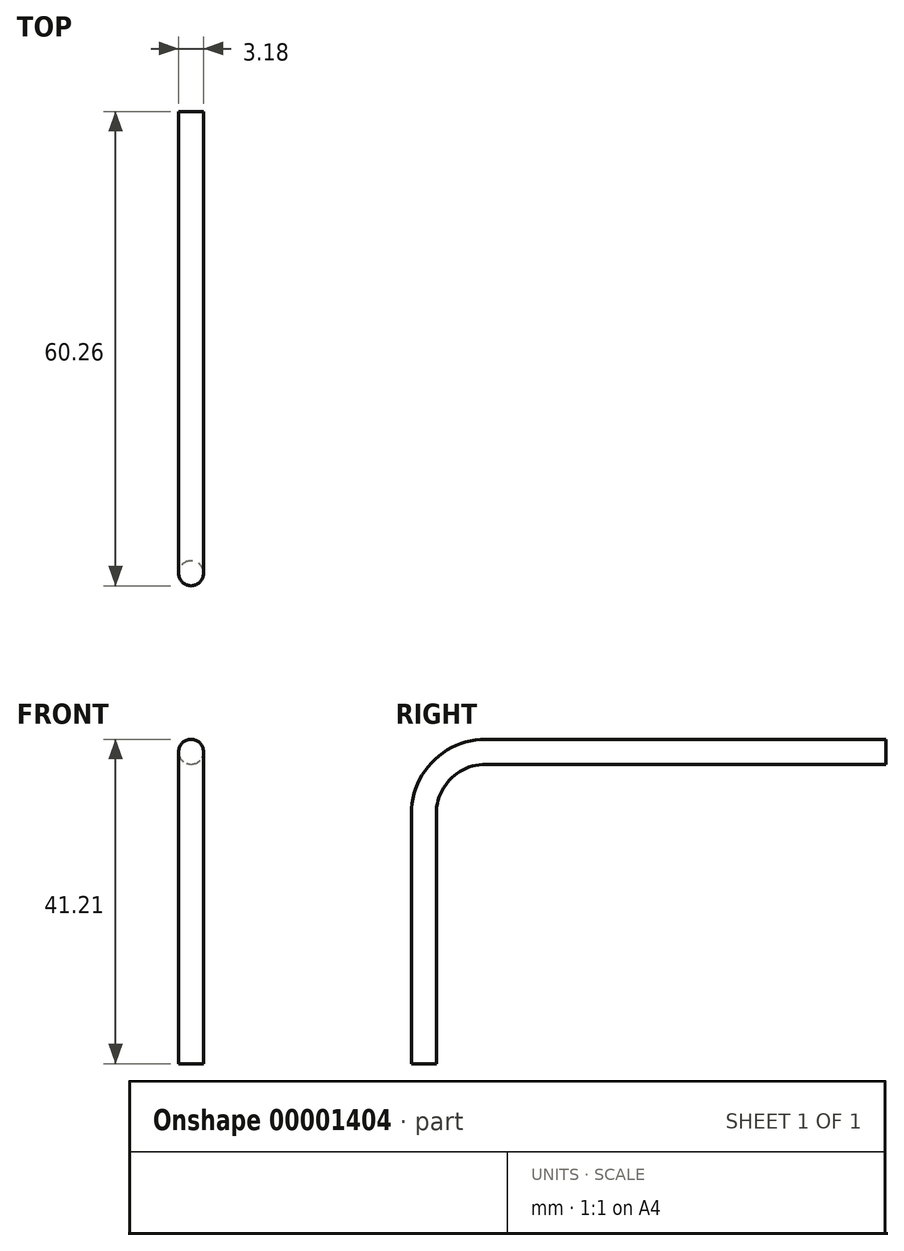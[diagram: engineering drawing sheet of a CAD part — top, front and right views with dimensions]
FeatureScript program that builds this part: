
annotation { "Feature Type Name" : "Feature", "Feature Type Description" : "" }
export const myFeature = defineFeature(function(context is Context, id is Id, definition is map)
    precondition{}
    {
        {
            var Q0;
            Q0=qCreatedBy(makeId("Right.planeOp"),FACE);
            var sketch = newSketch(context, id + "F0", { "sketchPlane" : qUnion([Q0])});
            skLineSegment(sketch, "E0", {"start": v(0, 0) * mm, "end": v(0, 31.75) * mm});
            skLineSegment(sketch, "E1", {"start": v(7.87, 39.62) * mm, "end": v(58.67, 39.62) * mm});
            skPoint(sketch, "E2.visualSharp", {"position": v(0, 39.62) * mm});
            skArc(sketch, "E2.filletArc", {"start": v(7.87, 39.62) * mm, "mid": v(2.3, 37.32) * mm, "end": v(0, 31.75) * mm});
            skSolve(sketch);
        }
        {
            var Q0;
            Q0=qCreatedBy(makeId("Top.planeOp"),FACE);
            var sketch = newSketch(context, id + "F1", { "sketchPlane" : qUnion([Q0])});
            skCircle(sketch, "E3", {"center": v(0, 0) * mm, "radius": 1.59 * mm});
            skSolve(sketch);
        }
        {
            var Q0;
            Q0 = qSketchRegion(id + "F1", true);
            var Q1;
            Q1=sQuery(id+"F0.wireOp",EDGE,"E0");
            var Q2;
            Q2=sQuery(id+"F0.wireOp",EDGE,"E2.filletArc");
            var Q3;
            Q3=sQuery(id+"F0.wireOp",EDGE,"E1");
            sweep(context, id + "F2", {"profiles" : qUnion([Q0]), "path" : qUnion([Q1, Q2, Q3])});
        }
    });
